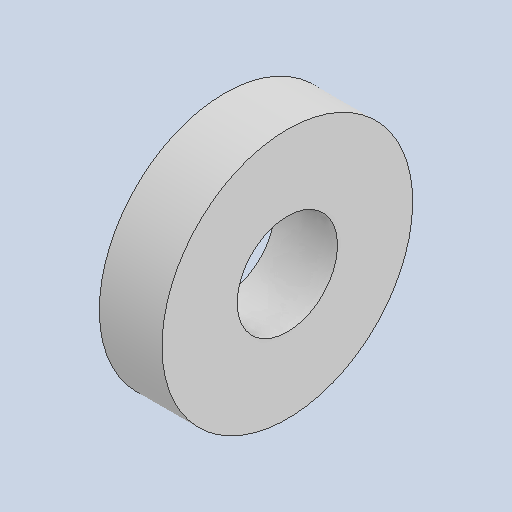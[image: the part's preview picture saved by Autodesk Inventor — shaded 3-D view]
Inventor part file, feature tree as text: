
AUTODESK INVENTOR PART (.ipt)
format: ipt  version: 2024 (Build 280153000, 153)  size: 92,160 bytes
history: native  units: in
note: dims shown in document units (in); Inventor stores cm internally (conversion verified against a paired STEP export)
features: other x3, sketch x1
ambient origin geometry x8: Origin, YZ Plane, XZ Plane, XY Plane, X Axis, Y Axis, Z Axis, Center Point
bodies: Solid1 (feature_tree)
feature tree (4):
  other  "part8.ipt"
  other  "Solid1::part8.ipt"
  other  "TaggingFeature1"
  sketch  "Sketch1"  dims[d0=0.3937in]
